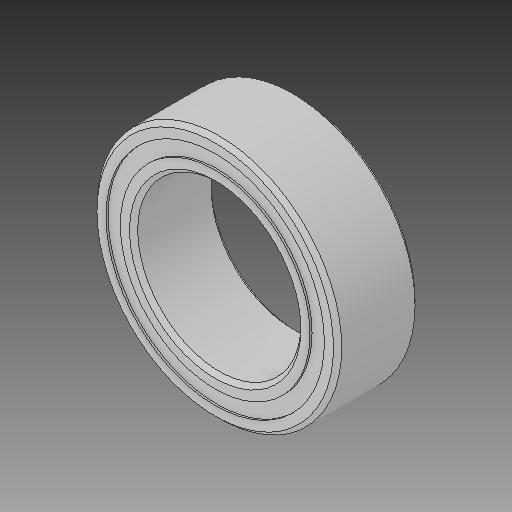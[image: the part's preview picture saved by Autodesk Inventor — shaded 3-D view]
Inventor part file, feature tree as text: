
AUTODESK INVENTOR PART (.ipt)
format: ipt  version: 2017 (Build 210142000, 142)  size: 608,256 bytes
history: native  units: in
note: dims shown in document units (in); Inventor stores cm internally (conversion verified against a paired STEP export)
features: other x11, revolve x5
ambient origin geometry x8: Origin, YZ Plane, XZ Plane, XY Plane, X Axis, Y Axis, Z Axis, Center Point
bodies: Solid1 (feature_tree), Solid2 (feature_tree), Solid3 (feature_tree), Solid4 (feature_tree), Solid5 (feature_tree), Solid6 (feature_tree), Solid7 (feature_tree), Solid8 (feature_tree), Solid9 (feature_tree), Solid10 (feature_tree), Solid11 (feature_tree), Solid12 (feature_tree), Solid13 (feature_tree), Solid14 (feature_tree), Solid15 (feature_tree), Solid16 (feature_tree)
feature tree (16):
  revolve  "Revolve1"  [1 undecoded]
  revolve  "Revolve3"  [1 undecoded]
  revolve  "Revolve4"  [1 undecoded]
  other  "CirPattern1[1]"
  other  "CirPattern1[2]"
  other  "CirPattern1[3]"
  other  "CirPattern1[4]"
  other  "CirPattern1[5]"
  other  "CirPattern1[6]"
  other  "CirPattern1[7]"
  other  "CirPattern1[8]"
  other  "CirPattern1[9]"
  other  "CirPattern1[10]"
  other  "CirPattern1[11]"
  revolve  "Revolve5[1]"  [1 undecoded]
  revolve  "Revolve5[2]"  [1 undecoded]
note: 5 required parameter values undecoded (feature->parameter linkage not recoverable at this tier; creation-order binding heuristic only, values carry confidence <= 0.55)
